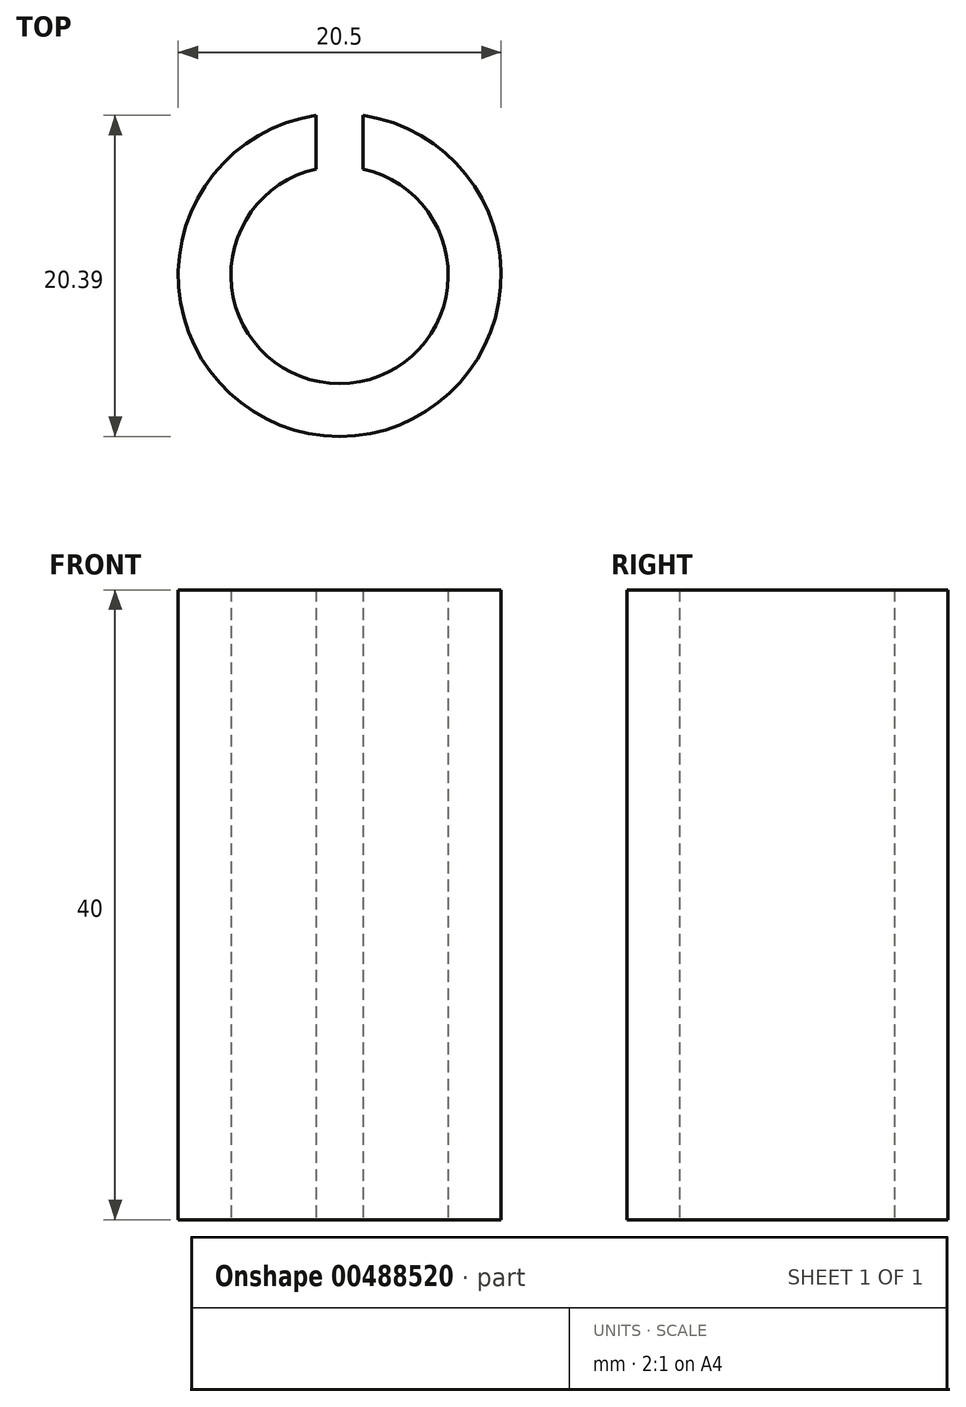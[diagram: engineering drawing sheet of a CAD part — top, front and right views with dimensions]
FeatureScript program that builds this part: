
annotation { "Feature Type Name" : "Feature", "Feature Type Description" : "" }
export const myFeature = defineFeature(function(context is Context, id is Id, definition is map)
    precondition{}
    {
        {
            var Q0;
            Q0=qCreatedBy(makeId("Top.planeOp"),FACE);
            var sketch = newSketch(context, id + "F0", { "sketchPlane" : qUnion([Q0])});
            skArc(sketch, "E0", {"start": v(-1.5, 10.14) * mm, "mid": v(0, -10.25) * mm, "end": v(1.5, 10.14) * mm});
            skArc(sketch, "E1", {"start": v(-1.5, 6.73) * mm, "mid": v(0, -6.9) * mm, "end": v(1.5, 6.73) * mm});
            skLineSegment(sketch, "E2", {"start": v(-1.5, 6.73) * mm, "end": v(-1.5, 10.14) * mm});
            skLineSegment(sketch, "E3", {"start": v(1.5, 10.14) * mm, "end": v(1.5, 6.73) * mm});
            skSolve(sketch);
        }
        {
            var Q0;
            Q0=makeQuery(id+"F0.imprint","IMPRINT",FACE,{"disambiguationData":[TD([[makeQuery(id+"F0.imprint","IMPRINT",EDGE,{"derivedFrom":sQuery(id+"F0.wireOp",EDGE,"E0")}),1.0]])]});
            extrude(context, id + "F1", {"entities" : qUnion([Q0]), "depth" : 40 * mm});
        }
    });
